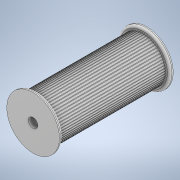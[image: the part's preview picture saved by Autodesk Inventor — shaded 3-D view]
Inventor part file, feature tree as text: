
AUTODESK INVENTOR PART (.ipt)
format: ipt  version: 2020 (Build 240168000, 168)  size: 265,216 bytes
history: mixed  units: in
note: dims shown in document units (in); Inventor stores cm internally (conversion verified against a paired STEP export)
features: fillet x1, imported_body x1
ambient origin geometry x8: Origin, YZ Plane, XZ Plane, XY Plane, X Axis, Y Axis, Z Axis, Center Point
bodies: Solid1 (imported_parasolid)
feature tree (2):
  fillet  "Fillet1"  [1 undecoded]
  imported_body  NMx_Import_Brep_tag  [imported B-rep: ~129 faces, bbox_mm=[44.4, 37.662953, 96.0]]
note: 1 required parameter value undecoded (feature->parameter linkage not recoverable at this tier; creation-order binding heuristic only, values carry confidence <= 0.55)
